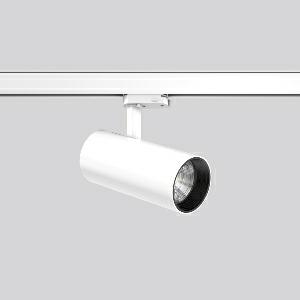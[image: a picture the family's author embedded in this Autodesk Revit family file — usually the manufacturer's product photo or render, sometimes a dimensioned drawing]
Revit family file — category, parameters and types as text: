
# Revit family: deecos_s_mini_742207_002_1_76_d14d
name_source: partatom
category: Lighting Fixtures
units: mm (PartAtom-declared; Revit-internal decimal feet)

## family parameters
Cut with Voids When Loaded = No
Host = Face
Light Source = No
Part Type = Normal
Room Calculation Point = No
Round Connector Dimension = Use Diameter
Shared = No

## types (1)
- DEECOS S mini (1 x LED Modul 940, 3200 lm, 4000)
    Apparent Load = 29 VA
    Approval mark = CE
    CIE Flux Codes = 96 100 100 100 100
    Color Rendering = 92
    Color Temperature = 4000
    Default Elevation = 1800 mm
    Description = Series: DEECOS S mini
LED surface-mounted projector in modern design with no visible cooling ribs. Housing: die-cast aluminium, powder-coated. Rotation range: 356°. Swivel range: 90°. Black plastic ring and recessed LED to prevent glare from the side. Optical assembly with lens made of plastic (polycarbonate) for the best homogeneous light distribution - can be changed without tools. Best colour rendering index Ra>90. With adapter for RZB 3-circuit DALI tracks. Suitable for Track on ceiling, Wall track. High quality converter without flickering and stroboscopic effect. The following accessories can be mounted without use of tools: interchangeable lenses, decorative glasses, honeycomb louvre, clear and frosted diffusers, white interchangeable plastic ring. 
Colour: traffic white, matt (RAL 9016)
Diameter: 87 mm
Height: 214 mm
Lamp: LED
Socket: without socket
Colour temperature: 4000K
Colour rendering index (CRI): 92
System power: 29 W
Rated luminous flux: 3200 lm
Luminous efficiency: 110 lm/W
Control gear: Converter, dimmable, DALI
Protection class: I
Type of protection: IP 20
    Height = 214 mm
    Lamp = 1 x LED Modul 940
    Lamp Light Flux = 3200 lm
    Lamp count = 1
    Length = 87 mm
    Lifetime = 50000 h
    Luminous efficacy = 110 lm/W
    Manufacturer = RZB
    ModVariant = No
    Model = 742207.002.1.76
    Mounting Place = Ceiling
    Mounting Type = Rail mounted
    Number of Poles = 1
    OnlyDefault = Yes
    Power Factor = 1
    Product Name = DEECOS S mini
    Product group = Track mounted projectors
    ProductGroupID = 301
    Protection Class = Protection class I
    Protection Degree = IP 20
    RLX_Detail_Level = 1
    RLX_Emergency_Light_Flux = 0 lm
    RLX_Emergency_Type = 0
    RLX_Emergency_Type_DB = No
    RlxData = <blob elided: 35429 chars, md5=cb095d2f>
    Socket = socket
    Standby Power = 0 W
    System Light Flux = 3200 lm
    System Power = 29 W
    Type Comments = Product without accessories
    Type Image = 741930.002.jpg
    URL = http://relux.com
    VarID = ---
    Voltage = 230 V
    Voltage Range = 220-240 V
    Weight = 0.00 kg
    Width = 0 mm  [stored 0 ft]

note: [stored X ft] marks values corroborated as IEEE doubles in the binary element streams (Revit-internal decimal feet)

## geometry (parser evidence)
native form markers: Blend x4, Sweep x13
no freeform markers — native parametric forms only
